# Revit family: Single Handle Bath & Shower Mixer_TOTO_TBG02302
name_source: partatom
category: 衛生器具
revit_build: Autodesk Revit 2018 (Build: 20170223_1515(x64)
units: mm (PartAtom-declared; Revit-internal decimal feet)

## family parameters
OmniClass タイトル = Sanitary, Laundry, and Cleaning Equipment
OmniClass 番号 = 23.45.00.00
パーツ タイプ = 標準
ロード時にボイドで切り取り = いいえ
丸型コネクタ寸法 = 直径を使用
作業面ベース = いいえ
共有 = いいえ
常に垂直 = はい
部屋計算ポイント = いいえ

## types (1)
- Single Handle Bath & Shower Mixer_TOTO_TBG02302
    Finish = faucet_material
    Height = 106.3  [stored 0.348753 ft]
    Length = 192  [stored 0.629921 ft]
    TOTO AsiaOceania = TBG02302B
    TOTO AsiaOceania URL = http://asia.toto.com
    TOTO China = TBG02302B
    TOTO China URL = http://www.toto.com.cn
    TOTO HongKong = TBG02302B
    TOTO HongKong URL = http://hk.toto.com
    TOTO India = TBG02302B
    TOTO India URL = https://in.toto.com
    TOTO Korea = TBG02302B
    TOTO Korea URL = https://kr.toto.com
    TOTO Taiwan = TBG02302P1/TBG02302P2
    TOTO Taiwan URL = https://www.twtoto.com.tw
    TOTO Taiwan URL 02 = https://www.twtoto.com.tw
    TOTO Taiwan URL 03 = https://www.twtoto.com.tw
    TOTO Taiwan URL 04 = https://www.twtoto.com.tw
    TOTO Thailand = TBG02302T
    TOTO Thailand URL = https://th.toto.com
    TOTO Vietnam = TBG02302V
    TOTO Vietnam URL = https://vn.toto.com
    TOTO Vietnam URL 02 = https://vn.toto.com
    TOTO Vietnam URL 03 = https://vn.toto.com
    TOTO Vietnam URL 04 = https://vn.toto.com
    TOTO Vietnam URL 05 = https://vn.toto.com
    TOTO Vietnam URL 06 = https://vn.toto.com
    TOTO Vietnam URL 07 = https://vn.toto.com
    TOTO Vietnam URL 08 = https://vn.toto.com
    TOTO Vietnam URL 09 = https://vn.toto.com
    Width = 215
    モデル = TBG02302
    製造元 = TOTO Ltd.
    説明 = Single Handle Bath & Shower Mixer/单柄双控浴缸水嘴

note: [stored X ft] marks values corroborated as IEEE doubles in the binary element streams (Revit-internal decimal feet)

## geometry (parser evidence)
native form markers: Sweep x2
no freeform markers — native parametric forms only
